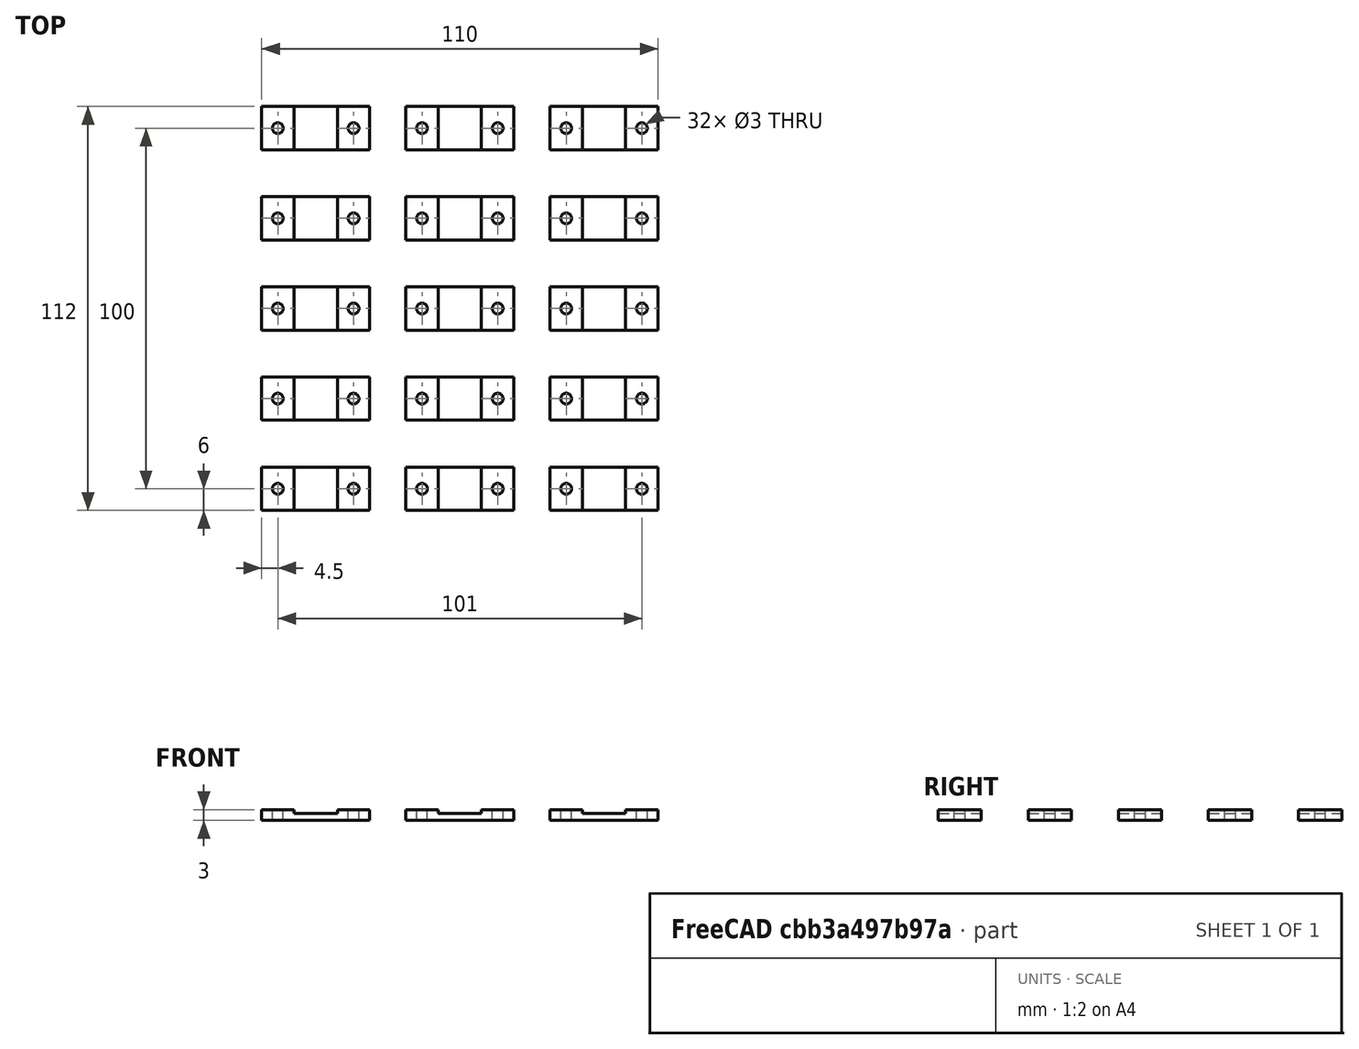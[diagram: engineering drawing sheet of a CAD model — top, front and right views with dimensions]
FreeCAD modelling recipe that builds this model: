
FCSTD DOCUMENT  (FreeCAD 0.17R13522 (Git))
Label: sujeta_botones
License: CreativeCommons Attribution-ShareAlike
LicenseURL: http://creativecommons.org/licenses/by-sa/4.0/
objects: Part::Cut×3, Part::Box×2, Part::Cylinder×2, Part::Feature×2, Part::FeaturePython×1
note: 10 computed .brp shape members not serialized (recipe doc carries the construction recipe); baked Part::Feature solids carry a one-line shape summary decoded from their .brp

FEATURE [Part::Box] Box  label="base"
  AttacherType = Attacher::AttachEngine3D
  Height = 3
  Length = 30
  Width = 12
FEATURE [Part::Box] Box001  label="posicion_para_boton"
  AttacherType = Attacher::AttachEngine3D
  Height = 1
  Length = 12
  Placement = pos=(9,0,2) rot=(0,0,1;0rad)
  Width = 12
FEATURE [Part::Cut] Cut
  Base = -> Box
  Refine = true
  Tool = -> Box001
FEATURE [Part::Cylinder] Cylinder
  Angle = 360
  AttacherType = Attacher::AttachEngine3D
  Height = 10
  Placement = pos=(25.5,6,-7) rot=(0,0,1;0rad)
  Radius = 1.5
FEATURE [Part::Cylinder] Cylinder001
  Angle = 360
  AttacherType = Attacher::AttachEngine3D
  Height = 10
  Placement = pos=(4.5,6,-7) rot=(0,0,1;0rad)
  Radius = 1.5
FEATURE [Part::Cut] Cut001
  Base = -> Cut
  Refine = true
  Tool = -> Cylinder001
FEATURE [Part::Feature] Cut002_solid001  label="Cut002 (Solid)001"
  shape: bbox 30 x 12 x 3 mm, 12 faces (baked)
FEATURE [Part::Feature] Cut002_solid  label="Cut002 (Solid)"
  shape: bbox 30 x 12 x 3 mm, 12 faces (baked)
FEATURE [Part::Cut] Cut002
  Base = -> Cut001
  Refine = true
  Tool = -> Cylinder
FEATURE [Part::FeaturePython] Array  # Draft array (typed FeaturePython)
  Angle = 360
  ArrayType = 0
  Axis = (0,0,1)
  Base = -> Cut002_solid001
  Center = (0,0,0)
  Fuse = false
  IntervalAxis = (0,0,0)
  IntervalX = (40,0,0)
  IntervalY = (0,25,0)
  IntervalZ = (0,0,0)
  NumberPolar = 1
  NumberX = 3
  NumberY = 5
  NumberZ = 1
